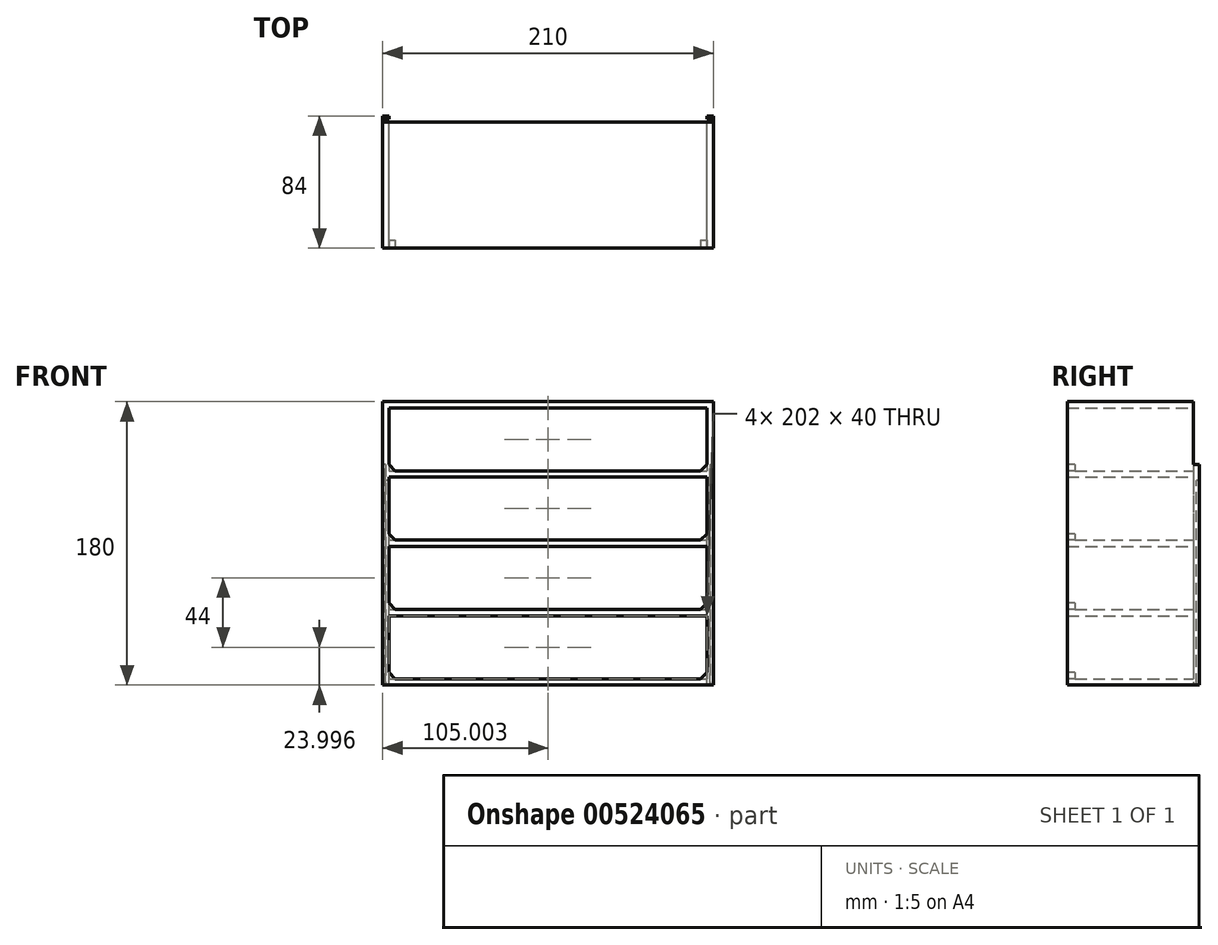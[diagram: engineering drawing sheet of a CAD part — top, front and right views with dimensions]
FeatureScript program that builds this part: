
annotation { "Feature Type Name" : "Feature", "Feature Type Description" : "" }
export const myFeature = defineFeature(function(context is Context, id is Id, definition is map)
    precondition{}
    {
        {
            var Q0;
            Q0=qCreatedBy(makeId("Front.planeOp"),FACE);
            var sketch = newSketch(context, id + "F0", { "sketchPlane" : qUnion([Q0])});
            skLineSegment(sketch, "E0.bottom", {"start": v(-113.9, 82.03) * mm, "end": v(96.1, 82.03) * mm});
            skLineSegment(sketch, "E0.top", {"start": v(-113.9, -97.97) * mm, "end": v(96.1, -97.97) * mm});
            skLineSegment(sketch, "E0.left", {"start": v(-113.9, 82.03) * mm, "end": v(-113.9, -97.97) * mm});
            skLineSegment(sketch, "E0.right", {"start": v(96.1, 82.03) * mm, "end": v(96.1, -97.97) * mm});
            skLineSegment(sketch, "E1.bottom", {"start": v(-109.9, 78.03) * mm, "end": v(92.1, 78.03) * mm});
            skLineSegment(sketch, "E1.top", {"start": v(-109.9, 38.03) * mm, "end": v(92.1, 38.03) * mm});
            skLineSegment(sketch, "E1.left", {"start": v(-109.9, 78.03) * mm, "end": v(-109.9, 38.03) * mm});
            skLineSegment(sketch, "E1.right", {"start": v(92.1, 78.03) * mm, "end": v(92.1, 38.03) * mm});
            skLineSegment(sketch, "E2.bottom", {"start": v(-109.9, 34.03) * mm, "end": v(92.1, 34.03) * mm});
            skLineSegment(sketch, "E2.top", {"start": v(-109.9, -5.97) * mm, "end": v(92.1, -5.97) * mm});
            skLineSegment(sketch, "E2.left", {"start": v(-109.9, 34.03) * mm, "end": v(-109.9, -5.97) * mm});
            skLineSegment(sketch, "E2.right", {"start": v(92.1, 34.03) * mm, "end": v(92.1, -5.97) * mm});
            skLineSegment(sketch, "E3.bottom", {"start": v(-109.9, -9.97) * mm, "end": v(92.1, -9.97) * mm});
            skLineSegment(sketch, "E3.top", {"start": v(-109.9, -49.97) * mm, "end": v(92.1, -49.97) * mm});
            skLineSegment(sketch, "E3.left", {"start": v(-109.9, -9.97) * mm, "end": v(-109.9, -49.97) * mm});
            skLineSegment(sketch, "E3.right", {"start": v(92.1, -9.97) * mm, "end": v(92.1, -49.97) * mm});
            skLineSegment(sketch, "E4.bottom", {"start": v(-109.9, -53.97) * mm, "end": v(92.1, -53.97) * mm});
            skLineSegment(sketch, "E4.top", {"start": v(-109.9, -93.97) * mm, "end": v(92.1, -93.97) * mm});
            skLineSegment(sketch, "E4.left", {"start": v(-109.9, -53.97) * mm, "end": v(-109.9, -93.97) * mm});
            skLineSegment(sketch, "E4.right", {"start": v(92.1, -53.97) * mm, "end": v(92.1, -93.97) * mm});
            skSolve(sketch);
        }
        {
            var Q0;
            Q0=makeQuery(id+"F0.imprint","IMPRINT",FACE,{"disambiguationData":[TD([[makeQuery(id+"F0.imprint","IMPRINT",EDGE,{"derivedFrom":sQuery(id+"F0.wireOp",EDGE,"E0.bottom")}),-1.0]])]});
            extrude(context, id + "F1", {"entities" : qUnion([Q0]), "depth" : 80 * mm, "offsetDistance" : 25 * mm});
        }
        {
            var Q0;
            Q0=makeQuery(id+"F1.opExtrude","SWEPT_FACE",FACE,{"disambiguationData":[OSD([sQuery(id+"F0.wireOp",EDGE,"E0.right")])]});
            var sketch = newSketch(context, id + "F2", { "sketchPlane" : qUnion([Q0])});
            skLineSegment(sketch, "E5.bottom", {"start": v(0, -97.97) * mm, "end": v(4, -97.97) * mm});
            skLineSegment(sketch, "E5.top", {"start": v(0, 42.03) * mm, "end": v(4, 42.03) * mm});
            skLineSegment(sketch, "E5.left", {"start": v(0, -97.97) * mm, "end": v(0, 42.03) * mm});
            skLineSegment(sketch, "E5.right", {"start": v(4, -97.97) * mm, "end": v(4, 42.03) * mm});
            skSolve(sketch);
        }
        {
            var Q0;
            Q0=makeQuery(id+"F2.imprint","IMPRINT",FACE,{"disambiguationData":[TD([[makeQuery(id+"F2.imprint","IMPRINT",EDGE,{"derivedFrom":sQuery(id+"F2.wireOp",EDGE,"E5.bottom")}),1.0]])]});
            extrude(context, id + "F3", {"entities" : qUnion([Q0]), "operationType" : NewBodyOperationType.ADD, "oppositeDirection" : true, "depth" : 2 * mm, "offsetDistance" : 25 * mm});
        }
        {
            var Q0;
            Q0=makeQuery(id+"F1.opExtrude","SWEPT_FACE",FACE,{"disambiguationData":[OSD([sQuery(id+"F0.wireOp",EDGE,"E0.left")])]});
            var sketch = newSketch(context, id + "F4", { "sketchPlane" : qUnion([Q0])});
            skLineSegment(sketch, "E6.bottom", {"start": v(0, -97.97) * mm, "end": v(-4, -97.97) * mm});
            skLineSegment(sketch, "E6.top", {"start": v(0, 42.03) * mm, "end": v(-4, 42.03) * mm});
            skLineSegment(sketch, "E6.left", {"start": v(0, -97.97) * mm, "end": v(0, 42.03) * mm});
            skLineSegment(sketch, "E6.right", {"start": v(-4, -97.97) * mm, "end": v(-4, 42.03) * mm});
            skSolve(sketch);
        }
        {
            var Q0;
            Q0 = qSketchRegion(id + "F4", true);
            extrude(context, id + "F5", {"entities" : qUnion([Q0]), "operationType" : NewBodyOperationType.ADD, "oppositeDirection" : true, "depth" : 2 * mm, "offsetDistance" : 25 * mm});
        }
        {
            var Q0;
            Q0=makeQuery(id+"F5.opExtrude","CAP_FACE",FACE,{"disambiguationData":[OSD([sQuery(id+"F4.wireOp",EDGE,"E6.bottom"),sQuery(id+"F4.wireOp",EDGE,"E6.top"),sQuery(id+"F4.wireOp",EDGE,"E6.left"),sQuery(id+"F4.wireOp",EDGE,"E6.right")])],"isStart":false});
            var sketch = newSketch(context, id + "F6", { "sketchPlane" : qUnion([Q0])});
            skLineSegment(sketch, "E7.bottom", {"start": v(4, -97.97) * mm, "end": v(2, -97.97) * mm});
            skLineSegment(sketch, "E7.top", {"start": v(4, 32.03) * mm, "end": v(2, 32.03) * mm});
            skLineSegment(sketch, "E7.left", {"start": v(4, -97.97) * mm, "end": v(4, 32.03) * mm});
            skLineSegment(sketch, "E7.right", {"start": v(2, -97.97) * mm, "end": v(2, 32.03) * mm});
            skSolve(sketch);
        }
        {
            var Q0;
            Q0 = qSketchRegion(id + "F6", true);
            extrude(context, id + "F7", {"entities" : qUnion([Q0]), "operationType" : NewBodyOperationType.ADD, "depth" : 2 * mm, "offsetDistance" : 25 * mm});
        }
        {
            var Q0;
            Q0=makeQuery(id+"F3.opExtrude","CAP_FACE",FACE,{"disambiguationData":[OSD([sQuery(id+"F2.wireOp",EDGE,"E5.bottom"),sQuery(id+"F2.wireOp",EDGE,"E5.top"),sQuery(id+"F2.wireOp",EDGE,"E5.left"),sQuery(id+"F2.wireOp",EDGE,"E5.right")])],"isStart":false});
            var sketch = newSketch(context, id + "F8", { "sketchPlane" : qUnion([Q0])});
            skLineSegment(sketch, "E8.bottom", {"start": v(-4, -97.97) * mm, "end": v(-2, -97.97) * mm});
            skLineSegment(sketch, "E8.top", {"start": v(-4, 32.03) * mm, "end": v(-2, 32.03) * mm});
            skLineSegment(sketch, "E8.left", {"start": v(-4, -97.97) * mm, "end": v(-4, 32.03) * mm});
            skLineSegment(sketch, "E8.right", {"start": v(-2, -97.97) * mm, "end": v(-2, 32.03) * mm});
            skSolve(sketch);
        }
        {
            var Q0;
            Q0=makeQuery(id+"F8.imprint","IMPRINT",FACE,{"disambiguationData":[TD([[makeQuery(id+"F8.imprint","IMPRINT",EDGE,{"derivedFrom":sQuery(id+"F8.wireOp",EDGE,"E8.bottom")}),-1.0]])]});
            extrude(context, id + "F9", {"entities" : qUnion([Q0]), "operationType" : NewBodyOperationType.ADD, "depth" : 2 * mm, "offsetDistance" : 25 * mm});
        }
        {
            var Q0;
            Q0=makeQuery(id+"F1.opExtrude","CAP_FACE",FACE,{"disambiguationData":[OSD([sQuery(id+"F0.wireOp",EDGE,"E0.bottom"),sQuery(id+"F0.wireOp",EDGE,"E0.top"),sQuery(id+"F0.wireOp",EDGE,"E0.left"),sQuery(id+"F0.wireOp",EDGE,"E0.right"),sQuery(id+"F0.wireOp",EDGE,"E1.bottom"),sQuery(id+"F0.wireOp",EDGE,"E1.top"),sQuery(id+"F0.wireOp",EDGE,"E1.left"),sQuery(id+"F0.wireOp",EDGE,"E1.right"),sQuery(id+"F0.wireOp",EDGE,"E2.bottom"),sQuery(id+"F0.wireOp",EDGE,"E2.top"),sQuery(id+"F0.wireOp",EDGE,"E2.left"),sQuery(id+"F0.wireOp",EDGE,"E2.right"),sQuery(id+"F0.wireOp",EDGE,"E3.bottom"),sQuery(id+"F0.wireOp",EDGE,"E3.top"),sQuery(id+"F0.wireOp",EDGE,"E3.left"),sQuery(id+"F0.wireOp",EDGE,"E3.right"),sQuery(id+"F0.wireOp",EDGE,"E4.bottom"),sQuery(id+"F0.wireOp",EDGE,"E4.top"),sQuery(id+"F0.wireOp",EDGE,"E4.left"),sQuery(id+"F0.wireOp",EDGE,"E4.right")])],"isStart":false});
            var sketch = newSketch(context, id + "F10", { "sketchPlane" : qUnion([Q0])});
            skLineSegment(sketch, "E9", {"start": v(-109.9, 38.03) * mm, "end": v(-109.9, 42.03) * mm});
            skLineSegment(sketch, "E10", {"start": v(-109.9, 38.03) * mm, "end": v(-105.9, 38.03) * mm});
            skLineSegment(sketch, "E11", {"start": v(-109.9, 42.03) * mm, "end": v(-105.9, 38.03) * mm});
            skLineSegment(sketch, "E12", {"start": v(-109.9, -49.97) * mm, "end": v(-109.9, -45.97) * mm});
            skLineSegment(sketch, "E13", {"start": v(-109.9, -49.97) * mm, "end": v(-105.9, -49.97) * mm});
            skLineSegment(sketch, "E14", {"start": v(-109.9, -45.97) * mm, "end": v(-105.9, -49.97) * mm});
            skLineSegment(sketch, "E15", {"start": v(-109.9, -93.97) * mm, "end": v(-109.9, -89.97) * mm});
            skLineSegment(sketch, "E16", {"start": v(-109.9, -93.97) * mm, "end": v(-105.9, -93.97) * mm});
            skLineSegment(sketch, "E17", {"start": v(-109.9, -89.97) * mm, "end": v(-105.9, -93.97) * mm});
            skLineSegment(sketch, "E18", {"start": v(92.1, -93.97) * mm, "end": v(88.1, -93.97) * mm});
            skLineSegment(sketch, "E19", {"start": v(88.1, -93.97) * mm, "end": v(92.1, -89.97) * mm});
            skLineSegment(sketch, "E20", {"start": v(92.1, -89.97) * mm, "end": v(92.1, -93.97) * mm});
            skLineSegment(sketch, "E21", {"start": v(92.1, -49.97) * mm, "end": v(88.1, -49.97) * mm});
            skLineSegment(sketch, "E22", {"start": v(88.1, -49.97) * mm, "end": v(92.1, -45.97) * mm});
            skLineSegment(sketch, "E23", {"start": v(92.1, -45.97) * mm, "end": v(92.1, -49.97) * mm});
            skLineSegment(sketch, "E24", {"start": v(-109.9, -5.97) * mm, "end": v(-105.9, -5.97) * mm});
            skLineSegment(sketch, "E25", {"start": v(-105.9, -5.97) * mm, "end": v(-109.9, -1.97) * mm});
            skLineSegment(sketch, "E26", {"start": v(-109.9, -1.97) * mm, "end": v(-109.9, -5.97) * mm});
            skLineSegment(sketch, "E27", {"start": v(92.1, -5.97) * mm, "end": v(88.1, -5.97) * mm});
            skLineSegment(sketch, "E28", {"start": v(88.1, -5.97) * mm, "end": v(92.1, -1.97) * mm});
            skLineSegment(sketch, "E29", {"start": v(92.1, -1.97) * mm, "end": v(92.1, -5.97) * mm});
            skLineSegment(sketch, "E30", {"start": v(92.1, 38.03) * mm, "end": v(88.1, 38.03) * mm});
            skLineSegment(sketch, "E31", {"start": v(88.1, 38.03) * mm, "end": v(92.1, 42.03) * mm});
            skLineSegment(sketch, "E32", {"start": v(92.1, 42.03) * mm, "end": v(92.1, 38.03) * mm});
            skSolve(sketch);
        }
        {
            var Q0;
            Q0=makeQuery(id+"F10.imprint","IMPRINT",FACE,{"disambiguationData":[TD([[makeQuery(id+"F10.imprint","IMPRINT",EDGE,{"derivedFrom":sQuery(id+"F10.wireOp",EDGE,"E12")}),1.0]])]});
            var Q1;
            Q1=makeQuery(id+"F10.imprint","IMPRINT",FACE,{"disambiguationData":[TD([[makeQuery(id+"F10.imprint","IMPRINT",EDGE,{"derivedFrom":sQuery(id+"F10.wireOp",EDGE,"E15")}),1.0]])]});
            var Q2;
            Q2=makeQuery(id+"F10.imprint","IMPRINT",FACE,{"disambiguationData":[TD([[makeQuery(id+"F10.imprint","IMPRINT",EDGE,{"derivedFrom":sQuery(id+"F10.wireOp",EDGE,"E18")}),1.0]])]});
            var Q3;
            Q3=makeQuery(id+"F10.imprint","IMPRINT",FACE,{"disambiguationData":[TD([[makeQuery(id+"F10.imprint","IMPRINT",EDGE,{"derivedFrom":sQuery(id+"F10.wireOp",EDGE,"E21")}),1.0]])]});
            var Q4;
            Q4=makeQuery(id+"F10.imprint","IMPRINT",FACE,{"disambiguationData":[TD([[makeQuery(id+"F10.imprint","IMPRINT",EDGE,{"derivedFrom":sQuery(id+"F10.wireOp",EDGE,"E24")}),1.0]])]});
            var Q5;
            Q5=makeQuery(id+"F10.imprint","IMPRINT",FACE,{"disambiguationData":[TD([[makeQuery(id+"F10.imprint","IMPRINT",EDGE,{"derivedFrom":sQuery(id+"F10.wireOp",EDGE,"E27")}),1.0]])]});
            var Q6;
            Q6=makeQuery(id+"F10.imprint","IMPRINT",FACE,{"disambiguationData":[TD([[makeQuery(id+"F10.imprint","IMPRINT",EDGE,{"derivedFrom":sQuery(id+"F10.wireOp",EDGE,"E30")}),1.0]])]});
            var Q7;
            Q7=makeQuery(id+"F10.imprint","IMPRINT",FACE,{"disambiguationData":[TD([[makeQuery(id+"F10.imprint","IMPRINT",EDGE,{"derivedFrom":sQuery(id+"F10.wireOp",EDGE,"E9")}),1.0]])]});
            extrude(context, id + "F11", {"entities" : qUnion([Q0, Q1, Q2, Q3, Q4, Q5, Q6, Q7]), "operationType" : NewBodyOperationType.ADD, "oppositeDirection" : true, "depth" : 5 * mm, "offsetDistance" : 25 * mm});
        }
    });
